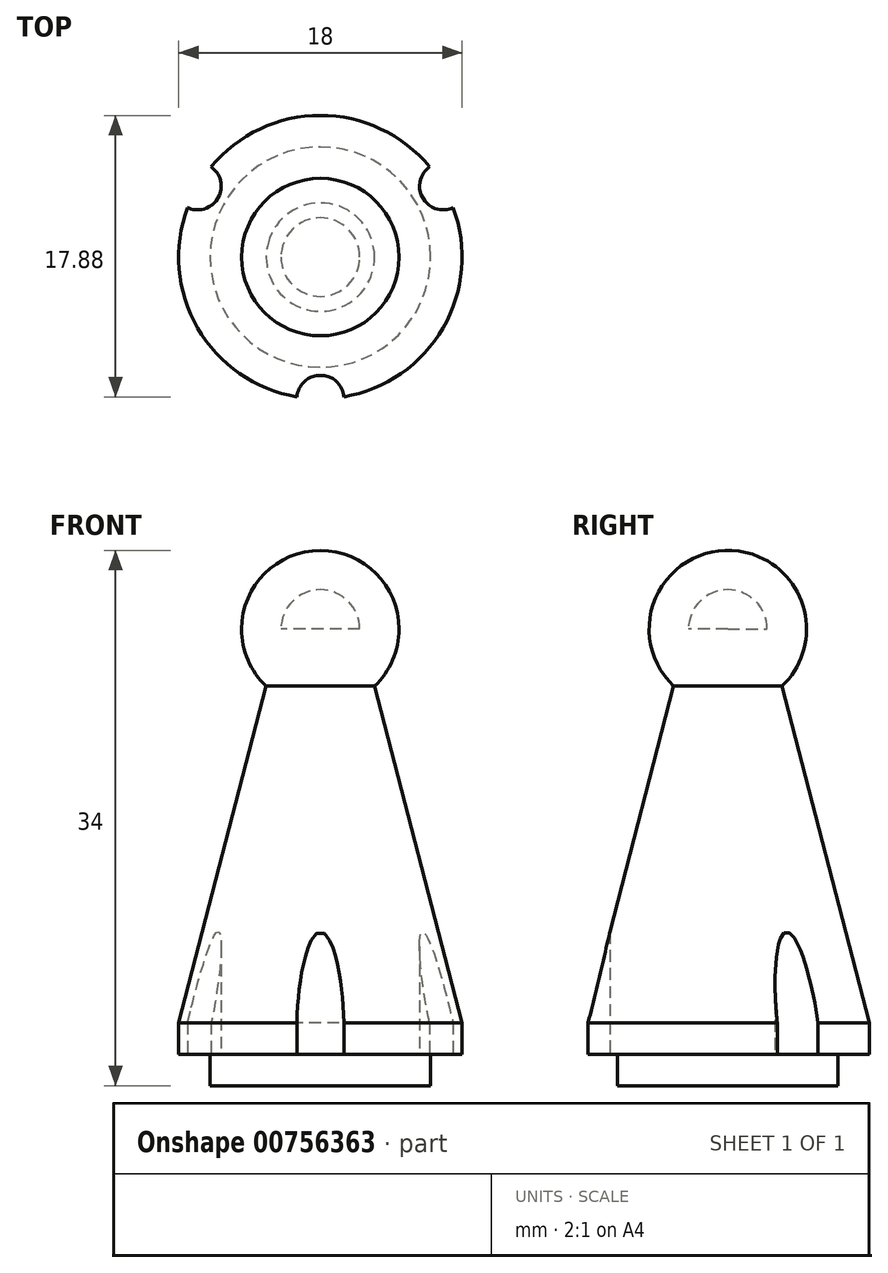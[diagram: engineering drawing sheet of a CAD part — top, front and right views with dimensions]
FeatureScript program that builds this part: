
annotation { "Feature Type Name" : "Feature", "Feature Type Description" : "" }
export const myFeature = defineFeature(function(context is Context, id is Id, definition is map)
    precondition{}
    {
        {
            var Q0;
            Q0=qCreatedBy(makeId("Top.planeOp"),FACE);
            var sketch = newSketch(context, id + "F0", { "sketchPlane" : qUnion([Q0])});
            skCircle(sketch, "E0", {"center": v(0, 0) * mm, "radius": 7 * mm});
            skSolve(sketch);
        }
        {
            var Q0;
            Q0 = qSketchRegion(id + "F0", true);
            extrude(context, id + "F1", {"entities" : qUnion([Q0]), "depth" : 2 * mm, "offsetDistance" : 25 * mm});
        }
        {
            var Q0;
            Q0=makeQuery(id+"F1.opExtrude","CAP_FACE",FACE,{"disambiguationData":[OSD([sQuery(id+"F0.wireOp",EDGE,"E0")])],"isStart":false});
            var sketch = newSketch(context, id + "F2", { "sketchPlane" : qUnion([Q0])});
            skCircle(sketch, "E1", {"center": v(0, 0) * mm, "radius": 9 * mm});
            skSolve(sketch);
        }
        {
            var Q0;
            Q0 = qSketchRegion(id + "F2", true);
            extrude(context, id + "F3", {"entities" : qUnion([Q0]), "operationType" : NewBodyOperationType.ADD, "depth" : 2 * mm, "offsetDistance" : 25 * mm});
        }
        {
            var Q0;
            Q0=makeQuery(id+"F3.opExtrude","CAP_FACE",FACE,{"disambiguationData":[OSD([sQuery(id+"F2.wireOp",EDGE,"E1")])],"isStart":false});
            cPlane(context, id + "F4", {"entities" : qUnion([Q0]), "cplaneType" : CPlaneType.OFFSET, "offset" : 25 * mm, "width" : 150 * mm, "height" : 150 * mm});
        }
        {
            var Q0;
            Q0=qCreatedBy(id+"F4.planeOp",FACE);
            var sketch = newSketch(context, id + "F5", { "sketchPlane" : qUnion([Q0])});
            skCircle(sketch, "E2", {"center": v(0, 0) * mm, "radius": 2.5 * mm});
            skSolve(sketch);
        }
        {
            var Q1;
            Q1=makeQuery(id+"F3.opExtrude","CAP_FACE",FACE,{"disambiguationData":[OSD([sQuery(id+"F2.wireOp",EDGE,"E1")])],"isStart":false});
            var Q2;
            Q2=makeQuery(id+"F5.imprint","IMPRINT",FACE,{"disambiguationData":[TD([[makeQuery(id+"F5.imprint","IMPRINT",EDGE,{"derivedFrom":sQuery(id+"F5.wireOp",EDGE,"E2")}),1.0]])]});
            loft(context, id + "F6", {"operationType" : NewBodyOperationType.ADD, "sheetProfilesArray" : [{ "sheetProfileEntities" : qUnion([Q1]) }, { "sheetProfileEntities" : qUnion([Q2]) }]});
        }
        {
            var Q0;
            Q0=makeQuery(id+"F6.opLoft","CAP_FACE",FACE,{"disambiguationData":[OSD([makeQuery(id+"F5.imprint","IMPRINT",FACE,{"disambiguationData":[TD([[makeQuery(id+"F5.imprint","IMPRINT",EDGE,{"derivedFrom":sQuery(id+"F5.wireOp",EDGE,"E2")}),1.0]])]})])],"isStart":true});
            var sketch = newSketch(context, id + "F7", { "sketchPlane" : qUnion([Q0])});
            skCircle(sketch, "E3", {"center": v(0, 0) * mm, "radius": 5 * mm});
            skLineSegment(sketch, "E4", {"start": v(-5, 0) * mm, "end": v(5, 0) * mm});
            skSolve(sketch);
        }
        {
            var Q0;
            {var subQ0=sQuery(id+"F7.wireOp",EDGE,"E4");var subQ1=sQuery(id+"F7.wireOp",EDGE,"E3");var subQ2=makeQuery(id+"F7.imprint","INTERSECT",VERTEX,{"disambiguationData":[OD(0.0)],"derivedFrom":[subQ1,subQ0]});Q0=makeQuery(id+"F7.imprint","IMPRINT",FACE,{"disambiguationData":[TD([[makeQuery(id+"F7.imprint","IMPRINT",EDGE,{"disambiguationData":[TD([[subQ2,1.0]])],"derivedFrom":subQ1}),1.0]])]});}
            var Q1;
            Q1=sQuery(id+"F7.wireOp",EDGE,"E4");
            revolve(context, id + "F8", {"operationType" : NewBodyOperationType.ADD, "surfaceOperationType" : NewSurfaceOperationType.NEW, "entities" : qUnion([Q0]), "axis" : qUnion([Q1]), "revolveType" : RevolveType.FULL});
        }
        {
            var Q0;
            Q0=makeQuery(id+"F3.opExtrude","CAP_FACE",FACE,{"disambiguationData":[OSD([sQuery(id+"F2.wireOp",EDGE,"E1")])],"isStart":true});
            var sketch = newSketch(context, id + "F9", { "sketchPlane" : qUnion([Q0])});
            skCircle(sketch, "E5", {"center": v(0, 9) * mm, "radius": 1.5 * mm});
            skCircle(sketch, "E6.1.0", {"center": v(-7.8, -4.5) * mm, "radius": 1.5 * mm});
            skCircle(sketch, "E6.2.0", {"center": v(7.8, -4.5) * mm, "radius": 1.5 * mm});
            skPoint(sketch, "E6.center", {"position": v(0, 0) * mm});
            skSolve(sketch);
        }
        {
            var Q0;
            {var subQ0=sQuery(id+"F9.wireOp",EDGE,"E5");var subQ1=makeQuery(id+"F3.opExtrude","CAP_EDGE",EDGE,{"disambiguationData":[OSD([sQuery(id+"F2.wireOp",EDGE,"E1")])],"isStart":true});var subQ2=makeQuery(id+"F9.imprint","INTERSECT",VERTEX,{"disambiguationData":[OD(0.0)],"derivedFrom":[subQ1,subQ0]});Q0=makeQuery(id+"F9.imprint","IMPRINT",FACE,{"disambiguationData":[TD([[makeQuery(id+"F9.imprint","IMPRINT",EDGE,{"disambiguationData":[TD([[subQ2,-1.0]])],"derivedFrom":subQ0}),1.0]])]});}
            var Q1;
            {var subQ0=sQuery(id+"F9.wireOp",EDGE,"E6.1.0");var subQ1=makeQuery(id+"F3.opExtrude","CAP_EDGE",EDGE,{"disambiguationData":[OSD([sQuery(id+"F2.wireOp",EDGE,"E1")])],"isStart":true});var subQ2=makeQuery(id+"F9.imprint","INTERSECT",VERTEX,{"disambiguationData":[OD(0.0)],"derivedFrom":[subQ1,subQ0]});Q1=makeQuery(id+"F9.imprint","IMPRINT",FACE,{"disambiguationData":[TD([[makeQuery(id+"F9.imprint","IMPRINT",EDGE,{"disambiguationData":[TD([[subQ2,1.0]])],"derivedFrom":subQ0}),1.0]])]});}
            var Q2;
            {var subQ0=sQuery(id+"F9.wireOp",EDGE,"E6.2.0");var subQ1=makeQuery(id+"F3.opExtrude","CAP_EDGE",EDGE,{"disambiguationData":[OSD([sQuery(id+"F2.wireOp",EDGE,"E1")])],"isStart":true});var subQ2=makeQuery(id+"F9.imprint","INTERSECT",VERTEX,{"disambiguationData":[OD(0.0)],"derivedFrom":[subQ1,subQ0]});Q2=makeQuery(id+"F9.imprint","IMPRINT",FACE,{"disambiguationData":[TD([[makeQuery(id+"F9.imprint","IMPRINT",EDGE,{"disambiguationData":[TD([[subQ2,1.0]])],"derivedFrom":subQ0}),1.0]])]});}
            var Q3;
            Q3=sQuery(id+"F9.wireOp",EDGE,"E5");
            var Q4;
            Q4=sQuery(id+"F9.wireOp",EDGE,"E6.2.0");
            var Q5;
            Q5=sQuery(id+"F9.wireOp",EDGE,"E6.1.0");
            extrude(context, id + "F10", {"entities" : qUnion([Q0, Q1, Q2]), "operationType" : NewBodyOperationType.REMOVE, "surfaceEntities" : qUnion([Q3, Q4, Q5]), "endBound" : BoundingType.THROUGH_ALL, "oppositeDirection" : true, "depth" : 25 * mm, "offsetDistance" : 25 * mm});
        }
    });
